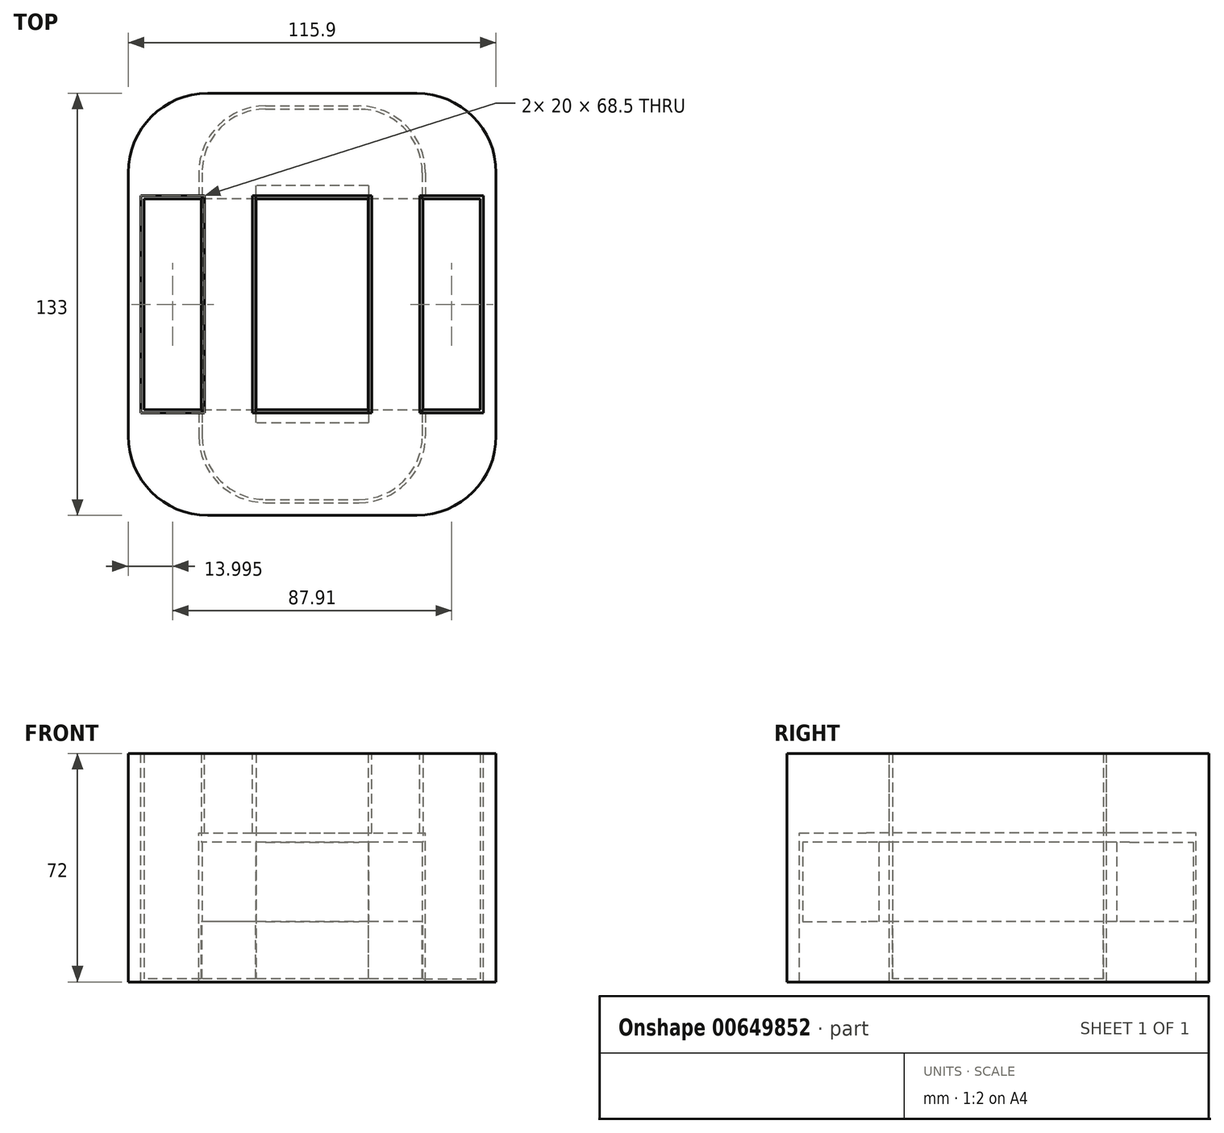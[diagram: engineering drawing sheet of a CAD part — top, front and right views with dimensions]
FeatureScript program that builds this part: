
annotation { "Feature Type Name" : "Feature", "Feature Type Description" : "" }
export const myFeature = defineFeature(function(context is Context, id is Id, definition is map)
    precondition{}
    {
        {
            var Q0;
            Q0=qCreatedBy(makeId("Top.planeOp"),FACE);
            var sketch = newSketch(context, id + "F0", { "sketchPlane" : qUnion([Q0])});
            skLineSegment(sketch, "E0.bottom", {"start": v(34.95, 33.25) * mm, "end": v(52.95, 33.25) * mm});
            skLineSegment(sketch, "E0.top", {"start": v(34.95, -33.25) * mm, "end": v(52.95, -33.25) * mm});
            skLineSegment(sketch, "E0.left", {"start": v(34.95, 33.25) * mm, "end": v(34.95, -33.25) * mm});
            skLineSegment(sketch, "E0.right", {"start": v(52.95, 33.25) * mm, "end": v(52.95, -33.25) * mm});
            skLineSegment(sketch, "E1.bottom", {"start": v(17.65, 33.25) * mm, "end": v(-17.65, 33.25) * mm});
            skLineSegment(sketch, "E1.top", {"start": v(17.65, -33.25) * mm, "end": v(-17.65, -33.25) * mm});
            skLineSegment(sketch, "E1.left", {"start": v(17.65, 33.25) * mm, "end": v(17.66, -33.25) * mm});
            skLineSegment(sketch, "E1.right", {"start": v(-17.65, 33.25) * mm, "end": v(-17.66, -33.25) * mm});
            skLineSegment(sketch, "E2.bottom", {"start": v(-34.95, 33.25) * mm, "end": v(-52.95, 33.25) * mm});
            skLineSegment(sketch, "E2.top", {"start": v(-34.95, -33.25) * mm, "end": v(-52.95, -33.25) * mm});
            skLineSegment(sketch, "E2.left", {"start": v(-34.95, 33.25) * mm, "end": v(-34.95, -33.25) * mm});
            skLineSegment(sketch, "E2.right", {"start": v(-52.95, 33.25) * mm, "end": v(-52.95, -33.25) * mm});
            skLineSegment(sketch, "E3.bottom", {"start": v(-14.7, 61.5) * mm, "end": v(14.7, 61.5) * mm});
            skLineSegment(sketch, "E3.top", {"start": v(-14.7, -61.5) * mm, "end": v(14.7, -61.5) * mm});
            skLineSegment(sketch, "E3.left", {"start": v(-34.7, 41.5) * mm, "end": v(-34.7, -41.5) * mm});
            skLineSegment(sketch, "E3.right", {"start": v(34.7, 41.5) * mm, "end": v(34.7, -41.5) * mm});
            skLineSegment(sketch, "E4.bottom", {"start": v(17.76, 37.45) * mm, "end": v(-17.76, 37.45) * mm});
            skLineSegment(sketch, "E4.top", {"start": v(17.76, -37.45) * mm, "end": v(-17.76, -37.45) * mm});
            skLineSegment(sketch, "E4.left", {"start": v(17.75, 37.45) * mm, "end": v(17.76, -37.45) * mm});
            skLineSegment(sketch, "E4.right", {"start": v(-17.75, 37.45) * mm, "end": v(-17.76, -37.45) * mm});
            skPoint(sketch, "E5.visualSharp", {"position": v(-34.7, 61.5) * mm});
            skArc(sketch, "E5.filletArc", {"start": v(-14.7, 61.5) * mm, "mid": v(-28.85, 55.64) * mm, "end": v(-34.7, 41.5) * mm});
            skPoint(sketch, "E6.visualSharp", {"position": v(34.7, 61.5) * mm});
            skArc(sketch, "E6.filletArc", {"start": v(34.7, 41.5) * mm, "mid": v(28.85, 55.64) * mm, "end": v(14.7, 61.5) * mm});
            skPoint(sketch, "E7.visualSharp", {"position": v(34.7, -61.5) * mm});
            skArc(sketch, "E7.filletArc", {"start": v(14.7, -61.5) * mm, "mid": v(28.85, -55.64) * mm, "end": v(34.7, -41.5) * mm});
            skPoint(sketch, "E8.visualSharp", {"position": v(-34.7, -61.5) * mm});
            skArc(sketch, "E8.filletArc", {"start": v(-34.7, -41.5) * mm, "mid": v(-28.85, -55.64) * mm, "end": v(-14.7, -61.5) * mm});
            skLineSegment(sketch, "E9", {"start": v(-34.95, -33.25) * mm, "end": v(-17.65, -33.25) * mm});
            skLineSegment(sketch, "E10", {"start": v(17.65, -33.25) * mm, "end": v(34.95, -33.25) * mm});
            skLineSegment(sketch, "E11", {"start": v(34.95, 33.25) * mm, "end": v(17.65, 33.25) * mm});
            skLineSegment(sketch, "E12", {"start": v(-17.65, 33.25) * mm, "end": v(-34.95, 33.25) * mm});
            skSolve(sketch);
        }
        {
            var Q0;
            Q0=makeQuery(id+"F0.imprint","IMPRINT",FACE,{"disambiguationData":[TD([[makeQuery(id+"F0.imprint","IMPRINT",EDGE,{"derivedFrom":sQuery(id+"F0.wireOp",EDGE,"E0.bottom")}),-1.0]])]});
            var Q1;
            Q1=makeQuery(id+"F0.imprint","IMPRINT",FACE,{"disambiguationData":[TD([[makeQuery(id+"F0.imprint","IMPRINT",EDGE,{"derivedFrom":sQuery(id+"F0.wireOp",EDGE,"E2.bottom")}),1.0]])]});
            var Q2;
            Q2=makeQuery(id+"F0.imprint","IMPRINT",FACE,{"disambiguationData":[TD([[makeQuery(id+"F0.imprint","IMPRINT",EDGE,{"derivedFrom":sQuery(id+"F0.wireOp",EDGE,"E1.bottom")}),1.0]])]});
            extrude(context, id + "F1", {"entities" : qUnion([Q0, Q1, Q2]), "depth" : 53 * mm, "offsetDistance" : 25 * mm});
        }
        {
            var Q0;
            Q0 = qSketchRegion(id + "F0", true);
            extrude(context, id + "F2", {"entities" : qUnion([Q0]), "operationType" : NewBodyOperationType.ADD, "depth" : 25 * mm, "offsetDistance" : 25 * mm});
        }
        {
            var Q0;
            {var subQ0=sQuery(id+"F0.wireOp",EDGE,"E11");var subQ1=sQuery(id+"F0.wireOp",EDGE,"E3.right");var subQ2=makeQuery(id+"F0.imprint","INTERSECT",VERTEX,{"derivedFrom":[subQ1,subQ0]});Q0=makeQuery(id+"F0.imprint","IMPRINT",FACE,{"disambiguationData":[TD([[makeQuery(id+"F0.imprint","IMPRINT",EDGE,{"disambiguationData":[TD([[subQ2,-1.0]])],"derivedFrom":subQ1}),-1.0]])]});}
            var Q1;
            Q1=makeQuery(id+"F0.imprint","IMPRINT",FACE,{"disambiguationData":[TD([[makeQuery(id+"F0.imprint","IMPRINT",EDGE,{"derivedFrom":sQuery(id+"F0.wireOp",EDGE,"E0.bottom")}),-1.0]])]});
            var Q2;
            Q2=makeQuery(id+"F0.imprint","IMPRINT",FACE,{"disambiguationData":[TD([[makeQuery(id+"F0.imprint","IMPRINT",EDGE,{"derivedFrom":sQuery(id+"F0.wireOp",EDGE,"E1.bottom")}),1.0]])]});
            var Q3;
            {var subQ0=sQuery(id+"F0.wireOp",EDGE,"E12");var subQ1=sQuery(id+"F0.wireOp",EDGE,"E3.left");var subQ2=makeQuery(id+"F0.imprint","INTERSECT",VERTEX,{"derivedFrom":[subQ1,subQ0]});Q3=makeQuery(id+"F0.imprint","IMPRINT",FACE,{"disambiguationData":[TD([[makeQuery(id+"F0.imprint","IMPRINT",EDGE,{"disambiguationData":[TD([[subQ2,-1.0]])],"derivedFrom":subQ1}),1.0]])]});}
            var Q4;
            Q4=makeQuery(id+"F0.imprint","IMPRINT",FACE,{"disambiguationData":[TD([[makeQuery(id+"F0.imprint","IMPRINT",EDGE,{"derivedFrom":sQuery(id+"F0.wireOp",EDGE,"E2.bottom")}),1.0]])]});
            extrude(context, id + "F3", {"entities" : qUnion([Q0, Q1, Q2, Q3, Q4]), "operationType" : NewBodyOperationType.ADD, "oppositeDirection" : true, "depth" : 18 * mm, "offsetDistance" : 25 * mm});
        }
        {
            var Q0;
            Q0=makeQuery(id+"F1.opExtrude","CAP_FACE",FACE,{"disambiguationData":[OSD([sQuery(id+"F0.wireOp",EDGE,"E1.bottom"),sQuery(id+"F0.wireOp",EDGE,"E1.top"),sQuery(id+"F0.wireOp",EDGE,"E1.left"),sQuery(id+"F0.wireOp",EDGE,"E1.right")])],"isStart":false});
            var sketch = newSketch(context, id + "F4", { "sketchPlane" : qUnion([Q0])});
            skLineSegment(sketch, "E13.bottom", {"start": v(-32.95, 66.5) * mm, "end": v(32.95, 66.5) * mm});
            skLineSegment(sketch, "E13.top", {"start": v(-32.95, -66.5) * mm, "end": v(32.95, -66.5) * mm});
            skLineSegment(sketch, "E13.left", {"start": v(-57.95, 41.5) * mm, "end": v(-57.95, -41.5) * mm});
            skLineSegment(sketch, "E13.right", {"start": v(57.95, 41.5) * mm, "end": v(57.95, -41.5) * mm});
            skPoint(sketch, "E14.visualSharp", {"position": v(-57.95, -66.5) * mm});
            skArc(sketch, "E14.filletArc", {"start": v(-57.95, -41.5) * mm, "mid": v(-50.63, -59.18) * mm, "end": v(-32.95, -66.5) * mm});
            skPoint(sketch, "E15.visualSharp", {"position": v(-57.95, 66.5) * mm});
            skArc(sketch, "E15.filletArc", {"start": v(-32.95, 66.5) * mm, "mid": v(-50.63, 59.18) * mm, "end": v(-57.95, 41.5) * mm});
            skPoint(sketch, "E16.visualSharp", {"position": v(57.95, 66.5) * mm});
            skArc(sketch, "E16.filletArc", {"start": v(57.95, 41.5) * mm, "mid": v(50.63, 59.18) * mm, "end": v(32.95, 66.5) * mm});
            skPoint(sketch, "E17.visualSharp", {"position": v(57.95, -66.5) * mm});
            skArc(sketch, "E17.filletArc", {"start": v(32.95, -66.5) * mm, "mid": v(50.63, -59.18) * mm, "end": v(57.95, -41.5) * mm});
            skLineSegment(sketch, "E18.bottom", {"start": v(-53.95, 34.25) * mm, "end": v(-33.95, 34.25) * mm});
            skLineSegment(sketch, "E18.top", {"start": v(-53.95, -34.25) * mm, "end": v(-33.95, -34.25) * mm});
            skLineSegment(sketch, "E18.left", {"start": v(-53.95, 34.25) * mm, "end": v(-53.95, -34.25) * mm});
            skLineSegment(sketch, "E18.right", {"start": v(-33.95, 34.25) * mm, "end": v(-33.95, -34.25) * mm});
            skLineSegment(sketch, "E19.bottom", {"start": v(-18.75, 34.25) * mm, "end": v(18.75, 34.25) * mm});
            skLineSegment(sketch, "E19.top", {"start": v(-18.75, -34.25) * mm, "end": v(18.75, -34.25) * mm});
            skLineSegment(sketch, "E19.left", {"start": v(-18.76, 34.25) * mm, "end": v(-18.75, -34.25) * mm});
            skLineSegment(sketch, "E19.right", {"start": v(18.75, 34.25) * mm, "end": v(18.76, -34.25) * mm});
            skLineSegment(sketch, "E20.bottom", {"start": v(33.95, 34.25) * mm, "end": v(53.95, 34.25) * mm});
            skLineSegment(sketch, "E20.top", {"start": v(33.95, -34.25) * mm, "end": v(53.95, -34.25) * mm});
            skLineSegment(sketch, "E20.left", {"start": v(33.95, 34.25) * mm, "end": v(33.95, -34.25) * mm});
            skLineSegment(sketch, "E20.right", {"start": v(53.95, 34.25) * mm, "end": v(53.95, -34.25) * mm});
            skLineSegment(sketch, "E21.0", {"start": v(35.7, -33.25) * mm, "end": v(35.7, -41.5) * mm});
            skLineSegment(sketch, "E21.1", {"start": v(-35.7, -33.25) * mm, "end": v(-35.7, -41.5) * mm});
            skArc(sketch, "E21.2", {"start": v(-35.7, -41.5) * mm, "mid": v(-29.55, -56.35) * mm, "end": v(-14.7, -62.5) * mm});
            skLineSegment(sketch, "E21.3", {"start": v(-14.7, -62.5) * mm, "end": v(14.7, -62.5) * mm});
            skArc(sketch, "E21.4", {"start": v(14.7, -62.5) * mm, "mid": v(29.55, -56.35) * mm, "end": v(35.7, -41.5) * mm});
            skLineSegment(sketch, "E22.0", {"start": v(-35.7, 41.5) * mm, "end": v(-35.7, 33.25) * mm});
            skLineSegment(sketch, "E22.1", {"start": v(35.7, 41.5) * mm, "end": v(35.7, 33.25) * mm});
            skArc(sketch, "E22.2", {"start": v(35.7, 41.5) * mm, "mid": v(29.55, 56.35) * mm, "end": v(14.7, 62.5) * mm});
            skLineSegment(sketch, "E22.3", {"start": v(-14.7, 62.5) * mm, "end": v(14.7, 62.5) * mm});
            skArc(sketch, "E22.4", {"start": v(-14.7, 62.5) * mm, "mid": v(-29.55, 56.35) * mm, "end": v(-35.7, 41.5) * mm});
            skSolve(sketch);
        }
        {
            var Q0;
            Q0=makeQuery(id+"F4.imprint","IMPRINT",FACE,{"disambiguationData":[TD([[makeQuery(id+"F4.imprint","IMPRINT",EDGE,{"derivedFrom":sQuery(id+"F4.wireOp",EDGE,"E13.bottom")}),-1.0]])]});
            var Q1;
            {var subQ7=sQuery(id+"F4.wireOp",EDGE,"E18.right");Q1=makeQuery(id+"F4.imprint","IMPRINT",FACE,{"disambiguationData":[TD([[makeQuery(id+"F4.imprint","IMPRINT",EDGE,{"derivedFrom":subQ7}),1.0]])]});}
            extrude(context, id + "F5", {"entities" : qUnion([Q0, Q1]), "oppositeDirection" : true, "depth" : 25 * mm, "offsetDistance" : 25 * mm});
        }
        {
            var Q0;
            Q0=makeQuery(id+"F4.imprint","IMPRINT",FACE,{"disambiguationData":[TD([[makeQuery(id+"F4.imprint","IMPRINT",EDGE,{"derivedFrom":sQuery(id+"F4.wireOp",EDGE,"E13.bottom")}),-1.0]])]});
            extrude(context, id + "F6", {"entities" : qUnion([Q0]), "operationType" : NewBodyOperationType.ADD, "oppositeDirection" : true, "depth" : 72 * mm, "offsetDistance" : 25 * mm});
        }
        {
            var Q0;
            Q0=makeQuery(id+"F5.opExtrude","SWEPT_BODY",BODY,{"disambiguationData":[OSD([sQuery(id+"F4.wireOp",EDGE,"E13.bottom"),sQuery(id+"F4.wireOp",EDGE,"E13.top"),sQuery(id+"F4.wireOp",EDGE,"E13.left"),sQuery(id+"F4.wireOp",EDGE,"E13.right"),sQuery(id+"F4.wireOp",EDGE,"E14.filletArc"),sQuery(id+"F4.wireOp",EDGE,"E15.filletArc"),sQuery(id+"F4.wireOp",EDGE,"E16.filletArc"),sQuery(id+"F4.wireOp",EDGE,"E17.filletArc"),sQuery(id+"F4.wireOp",EDGE,"E18.bottom"),sQuery(id+"F4.wireOp",EDGE,"E18.top"),sQuery(id+"F4.wireOp",EDGE,"E18.left"),sQuery(id+"F4.wireOp",EDGE,"E18.right"),sQuery(id+"F4.wireOp",EDGE,"E19.bottom"),sQuery(id+"F4.wireOp",EDGE,"E19.top"),sQuery(id+"F4.wireOp",EDGE,"E19.left"),sQuery(id+"F4.wireOp",EDGE,"E19.right"),sQuery(id+"F4.wireOp",EDGE,"E20.bottom"),sQuery(id+"F4.wireOp",EDGE,"E20.top"),sQuery(id+"F4.wireOp",EDGE,"E20.left"),sQuery(id+"F4.wireOp",EDGE,"E20.right")])]});
            transform(context, id + "F7", {"entities" : qUnion([Q0]), "transformType" : TransformType.TRANSLATION_3D, "dx" : 0 * mm, "dy" : 0 * mm, "dz" : 0 * mm, "makeCopy" : true});
        }
    });
